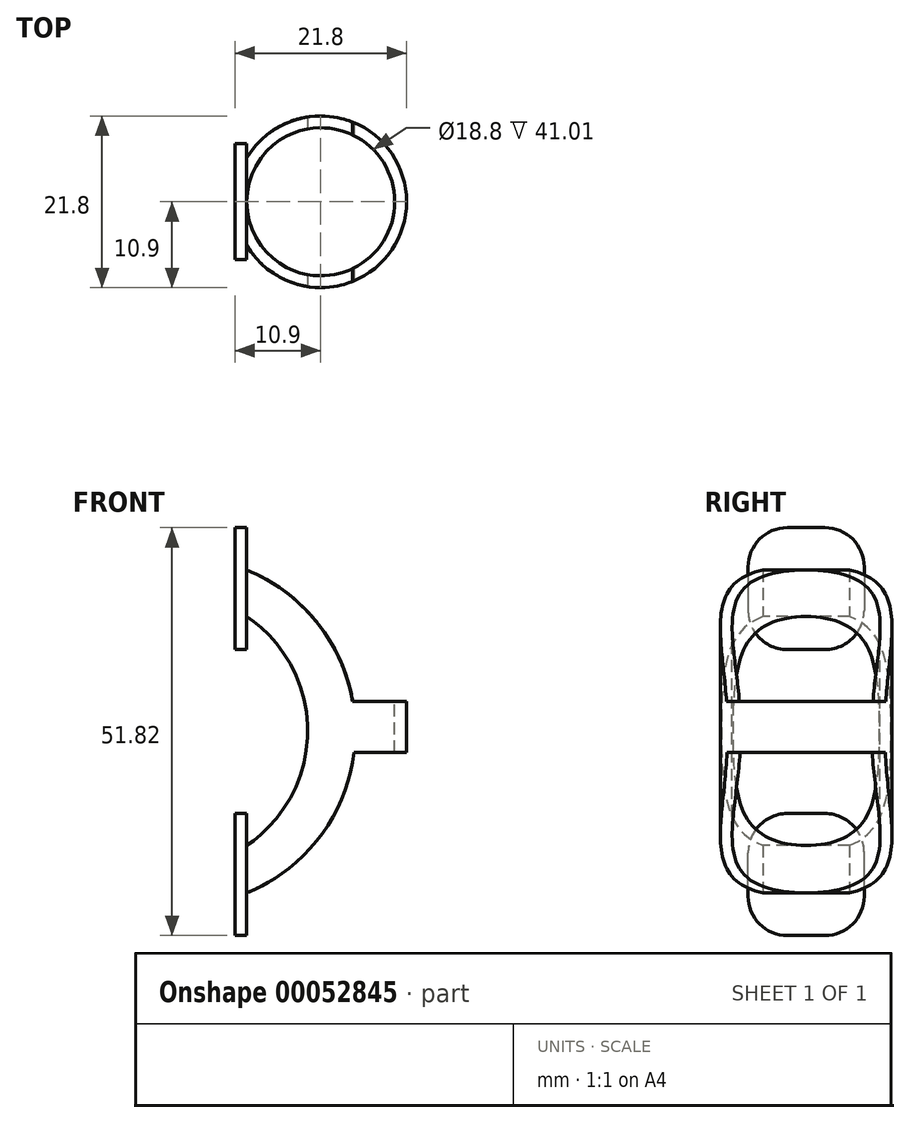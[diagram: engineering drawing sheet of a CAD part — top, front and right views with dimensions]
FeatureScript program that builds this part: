
annotation { "Feature Type Name" : "Feature", "Feature Type Description" : "" }
export const myFeature = defineFeature(function(context is Context, id is Id, definition is map)
    precondition{}
    {
        {
            var Q0;
            Q0=qCreatedBy(makeId("Top.planeOp"),FACE);
            var sketch = newSketch(context, id + "F0", { "sketchPlane" : qUnion([Q0])});
            skCircle(sketch, "E0", {"center": v(0, 0) * mm, "radius": 10.9 * mm});
            skSolve(sketch);
        }
        {
            var Q0;
            Q0=qSketchRegion(id+"F0",true);
            extrude(context, id + "F1", {"entities" : qUnion([Q0]), "depth" : 42 * mm});
        }
        {
            var Q0;
            Q0=makeQuery(id+"F1.opExtrude","CAP_FACE",FACE,{"disambiguationData":[OSD([sQuery(id+"F0.wireOp",EDGE,"E0")])],"isStart":false});
            var sketch = newSketch(context, id + "F2", { "sketchPlane" : qUnion([Q0])});
            skCircle(sketch, "E1.0", {"center": v(0, 0) * mm, "radius": 9.4 * mm});
            skSolve(sketch);
        }
        {
            var Q0;
            Q0=makeQuery(id+"F2.imprint","IMPRINT",FACE,{"disambiguationData":[TD([[makeQuery(id+"F2.imprint","IMPRINT",EDGE,{"derivedFrom":sQuery(id+"F2.wireOp",EDGE,"E1.0")}),1.0]])]});
            extrude(context, id + "F3", {"entities" : qUnion([Q0]), "operationType" : NewBodyOperationType.REMOVE, "endBound" : BoundingType.THROUGH_ALL, "oppositeDirection" : true, "depth" : 25 * mm});
        }
        {
            var Q0;
            Q0=qCreatedBy(makeId("Front.planeOp"),FACE);
            cPlane(context, id + "F4", {"entities" : qUnion([Q0]), "cplaneType" : CPlaneType.OFFSET, "offset" : 10.9 * mm, "width" : 150 * mm, "height" : 150 * mm});
        }
        {
            var Q0;
            Q0=qCreatedBy(makeId("Front.planeOp"),FACE);
            var sketch = newSketch(context, id + "F5", { "sketchPlane" : qUnion([Q0])});
            skArc(sketch, "E2", {"start": v(-11.41, 5.25) * mm, "mid": v(-1.67, 21.04) * mm, "end": v(-11.54, 36.75) * mm});
            skLineSegment(sketch, "E3", {"start": v(-11.54, 36.75) * mm, "end": v(-11.41, 5.25) * mm});
            skSolve(sketch);
        }
        {
            var Q0;
            Q0=makeQuery(id+"F5.imprint","IMPRINT",FACE,{"disambiguationData":[TD([[makeQuery(id+"F5.imprint","IMPRINT",EDGE,{"derivedFrom":sQuery(id+"F5.wireOp",EDGE,"E2")}),1.0]])]});
            extrude(context, id + "F6", {"entities" : qUnion([Q0]), "operationType" : NewBodyOperationType.REMOVE, "endBound" : BoundingType.SYMMETRIC, "oppositeDirection" : true, "depth" : 25 * mm});
        }
        {
            var Q0;
            Q0=qCreatedBy(id+"F4.planeOp",FACE);
            var sketch = newSketch(context, id + "F7", { "sketchPlane" : qUnion([Q0])});
            skArc(sketch, "E4", {"start": v(-10.48, 0) * mm, "mid": v(-0.51, 7.01) * mm, "end": v(4.23, 18.24) * mm});
            skLineSegment(sketch, "E5", {"start": v(4.06, 24.74) * mm, "end": v(19.03, 24.74) * mm});
            skLineSegment(sketch, "E6", {"start": v(19.03, 24.74) * mm, "end": v(19.03, 18.24) * mm});
            skLineSegment(sketch, "E7", {"start": v(19.03, 18.24) * mm, "end": v(4.23, 18.24) * mm});
            skArc(sketch, "E8.trimOffspring", {"start": v(4.06, 24.74) * mm, "mid": v(-1.2, 35.63) * mm, "end": v(-11.4, 42.12) * mm});
            skLineSegment(sketch, "E9", {"start": v(-11.4, 42.12) * mm, "end": v(25.8, 42.12) * mm});
            skLineSegment(sketch, "E10", {"start": v(25.8, 42.12) * mm, "end": v(25.8, 0) * mm});
            skLineSegment(sketch, "E11", {"start": v(25.8, 0) * mm, "end": v(-10.48, 0) * mm});
            skSolve(sketch);
        }
        {
            var Q0;
            Q0=makeQuery(id+"F7.imprint","IMPRINT",FACE,{"disambiguationData":[TD([[makeQuery(id+"F7.imprint","IMPRINT",EDGE,{"derivedFrom":sQuery(id+"F7.wireOp",EDGE,"E4")}),-1.0]])]});
            extrude(context, id + "F8", {"entities" : qUnion([Q0]), "operationType" : NewBodyOperationType.REMOVE, "endBound" : BoundingType.THROUGH_ALL, "oppositeDirection" : true, "depth" : 25 * mm});
        }
        {
            var Q0;
            Q0=qCreatedBy(makeId("Right.planeOp"),FACE);
            cPlane(context, id + "F9", {"entities" : qUnion([Q0]), "cplaneType" : CPlaneType.OFFSET, "offset" : 10.9 * mm, "oppositeDirection" : true, "width" : 150 * mm, "height" : 150 * mm});
        }
        {
            var Q0;
            Q0=qCreatedBy(id+"F9.planeOp",FACE);
            var sketch = newSketch(context, id + "F10", { "sketchPlane" : qUnion([Q0])});
            skLineSegment(sketch, "E12.bottom", {"start": v(2.37, 46.8) * mm, "end": v(-2.38, 46.8) * mm});
            skLineSegment(sketch, "E12.top", {"start": v(2.37, 31.3) * mm, "end": v(-2.38, 31.3) * mm});
            skLineSegment(sketch, "E12.left", {"start": v(7.37, 41.8) * mm, "end": v(7.37, 36.3) * mm});
            skLineSegment(sketch, "E12.right", {"start": v(-7.38, 41.8) * mm, "end": v(-7.38, 36.3) * mm});
            skLineSegment(sketch, "E13", {"start": v(2.13, 39.05) * mm, "end": v(-2.85, 39.05) * mm, "construction": true});
            skLineSegment(sketch, "E14", {"start": v(0, 41.08) * mm, "end": v(0, 36.65) * mm, "construction": true});
            skPoint(sketch, "E15.visualSharp", {"position": v(7.37, 46.8) * mm});
            skArc(sketch, "E15.filletArc", {"start": v(7.37, 41.8) * mm, "mid": v(5.91, 45.33) * mm, "end": v(2.37, 46.8) * mm});
            skPoint(sketch, "E16.visualSharp", {"position": v(-7.38, 46.8) * mm});
            skArc(sketch, "E16.filletArc", {"start": v(-2.38, 46.8) * mm, "mid": v(-5.91, 45.33) * mm, "end": v(-7.38, 41.8) * mm});
            skPoint(sketch, "E17.visualSharp", {"position": v(-7.38, 31.3) * mm});
            skArc(sketch, "E17.filletArc", {"start": v(-7.38, 36.3) * mm, "mid": v(-5.91, 32.76) * mm, "end": v(-2.38, 31.3) * mm});
            skPoint(sketch, "E18.visualSharp", {"position": v(7.38, 31.3) * mm});
            skArc(sketch, "E18.filletArc", {"start": v(2.37, 31.3) * mm, "mid": v(5.91, 32.76) * mm, "end": v(7.37, 36.3) * mm});
            skLineSegment(sketch, "E19", {"start": v(0, 20.9) * mm, "end": v(4.83, 20.9) * mm, "construction": true});
            skLineSegment(sketch, "E20.MirrorCS", {"start": v(7.37, -0.02) * mm, "end": v(7.37, 5.48) * mm});
            skArc(sketch, "E21.MirrorCS", {"start": v(7.37, -0.02) * mm, "mid": v(5.91, -3.55) * mm, "end": v(2.37, -5.02) * mm});
            skLineSegment(sketch, "E22.MirrorCS", {"start": v(2.37, -5.02) * mm, "end": v(-2.38, -5.02) * mm});
            skArc(sketch, "E23.MirrorCS", {"start": v(-2.38, -5.02) * mm, "mid": v(-5.91, -3.55) * mm, "end": v(-7.38, -0.02) * mm});
            skLineSegment(sketch, "E24.MirrorCS", {"start": v(-7.38, -0.02) * mm, "end": v(-7.38, 5.48) * mm});
            skArc(sketch, "E25.MirrorCS", {"start": v(-7.38, 5.48) * mm, "mid": v(-5.91, 9.02) * mm, "end": v(-2.38, 10.48) * mm});
            skLineSegment(sketch, "E26.MirrorCS", {"start": v(2.37, 10.48) * mm, "end": v(-2.38, 10.48) * mm});
            skArc(sketch, "E27.MirrorCS", {"start": v(2.37, 10.48) * mm, "mid": v(5.91, 9.02) * mm, "end": v(7.37, 5.48) * mm});
            skSolve(sketch);
        }
        {
            var Q0;
            Q0=makeQuery(id+"F10.imprint","IMPRINT",FACE,{"disambiguationData":[TD([[makeQuery(id+"F10.imprint","IMPRINT",EDGE,{"derivedFrom":sQuery(id+"F10.wireOp",EDGE,"E12.bottom")}),1.0]])]});
            var Q1;
            Q1=makeQuery(id+"F10.imprint","IMPRINT",FACE,{"disambiguationData":[TD([[makeQuery(id+"F10.imprint","IMPRINT",EDGE,{"derivedFrom":sQuery(id+"F10.wireOp",EDGE,"E20.MirrorCS")}),1.0]])]});
            extrude(context, id + "F11", {"entities" : qUnion([Q0, Q1]), "operationType" : NewBodyOperationType.ADD, "depth" : 1.5 * mm});
        }
    });
